# Revit family: PLANK_BENCH_TABLE
name_source: partatom
category: Arredi
units: mm (PartAtom-declared; Revit-internal decimal feet)

## family parameters
Condiviso = No
Host = Superficie
Punto di calcolo locali = No
Taglio con vuoti quando caricato = No

## types (4) — shared parameters
AVAILABLE FINISHES = Glides in plastic or felt.
BADGE = https://bim.archiproducts.com
COLLECTION = Bench
Descrizione = Table from wood with Quick-assembly system
HEIGHT = 600 mm
LENGTH = 2200 mm
MATERIAL DESCRIPTION = Table top and sides in solid wood, spruce oiled. Wood elements connected by a quick assembly system.
Modello = BENCH
PRODUCT SHEET = https://www.archiproducts.com
Produttore = PLANK
Prospetto di default = 1219 mm
STRUCTURE MATERIAL = PLANK_WOOD_NATURAL
TECHNICAL SHEET = https://www.plank.it
URL = https://www.plank.it

## per-type parameters (varying)
| type | PRODUCT CODE | VISIBILITY CENTER DX | VISIBILITY CENTER SX | VISIBILITY DX | VISIBILITY SX | WIDTH |
| 0660-01 NATURAL | 0660-01 | No | No | Sì | Sì | 600 mm |
| 0661-01 NATURAL | 0661-01 | Sì | No | No | Sì | 600 mm |
| 0662-01 NATURAL | 0662-01 | Sì | Sì | No | No | 600 mm |
| 0682-01 NATURAL | 0682-01 | Sì | Sì | No | No | 800 mm |
